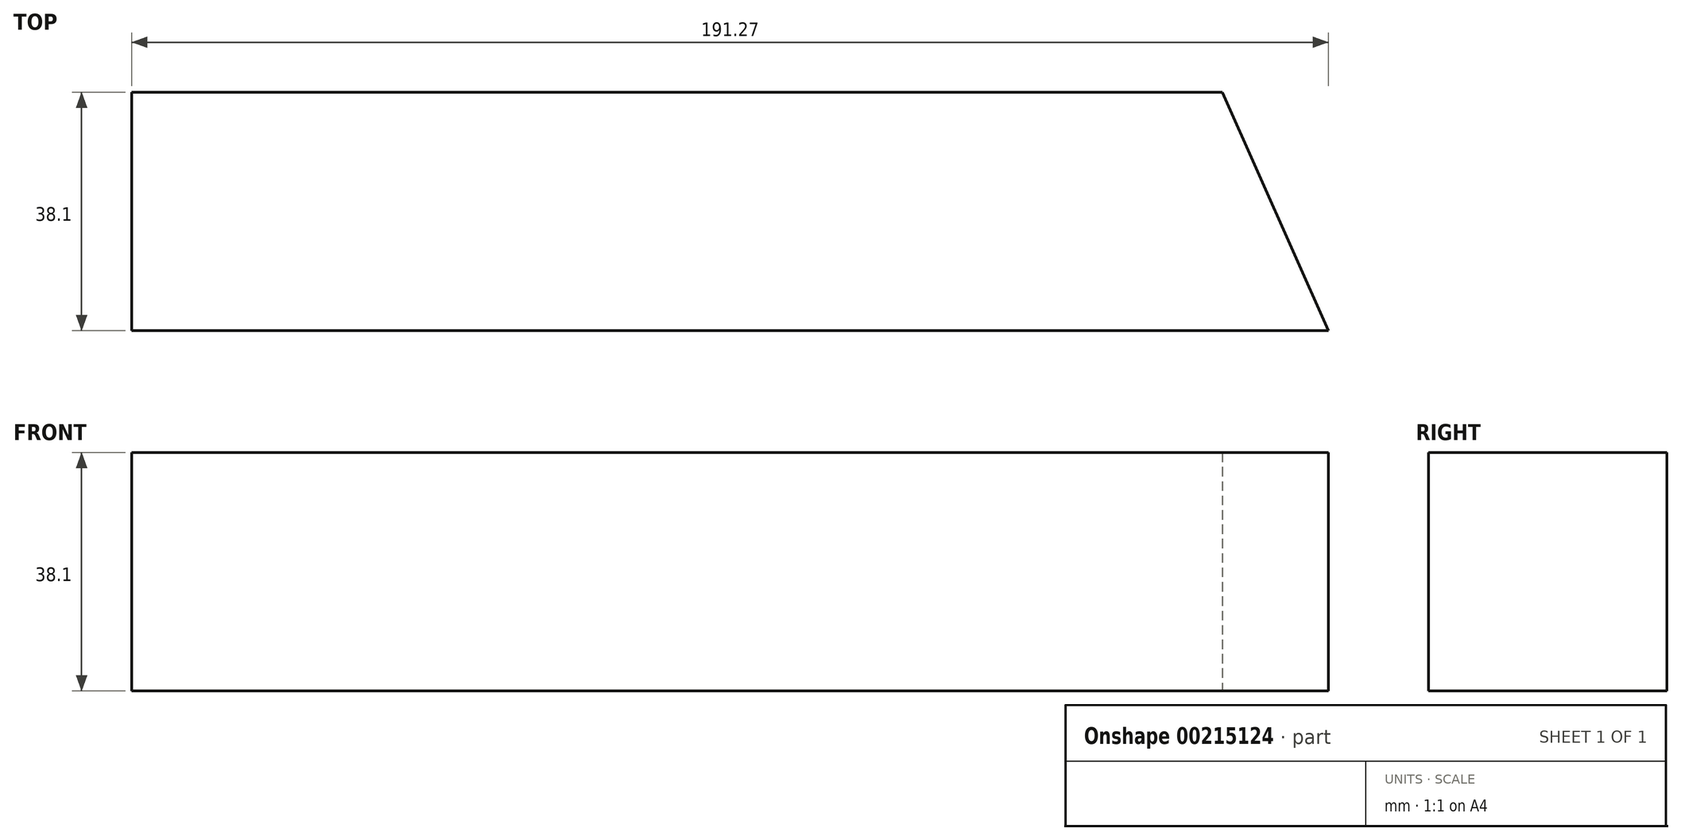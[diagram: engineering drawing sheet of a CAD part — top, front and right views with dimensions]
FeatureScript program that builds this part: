
annotation { "Feature Type Name" : "Feature", "Feature Type Description" : "" }
export const myFeature = defineFeature(function(context is Context, id is Id, definition is map)
    precondition{}
    {
        {
            var Q0;
            Q0=qCreatedBy(makeId("Top.planeOp"),FACE);
            var sketch = newSketch(context, id + "F0", { "sketchPlane" : qUnion([Q0])});
            skLineSegment(sketch, "E0", {"start": v(0, 0) * mm, "end": v(191.27, 0) * mm});
            skLineSegment(sketch, "E1", {"start": v(191.27, 0) * mm, "end": v(174.3, 38.1) * mm});
            skLineSegment(sketch, "E2", {"start": v(174.3, 38.1) * mm, "end": v(0, 38.1) * mm});
            skLineSegment(sketch, "E3", {"start": v(0, 38.1) * mm, "end": v(0, 0) * mm});
            skSolve(sketch);
        }
        {
            var Q0;
            Q0=makeQuery(id+"F0.imprint","IMPRINT",FACE,{"disambiguationData":[TD([[makeQuery(id+"F0.imprint","IMPRINT",EDGE,{"derivedFrom":sQuery(id+"F0.wireOp",EDGE,"E0")}),1.0]])]});
            extrude(context, id + "F1", {"entities" : qUnion([Q0]), "depth" : 38.1 * mm, "offsetDistance" : 25.4 * mm});
        }
    });
